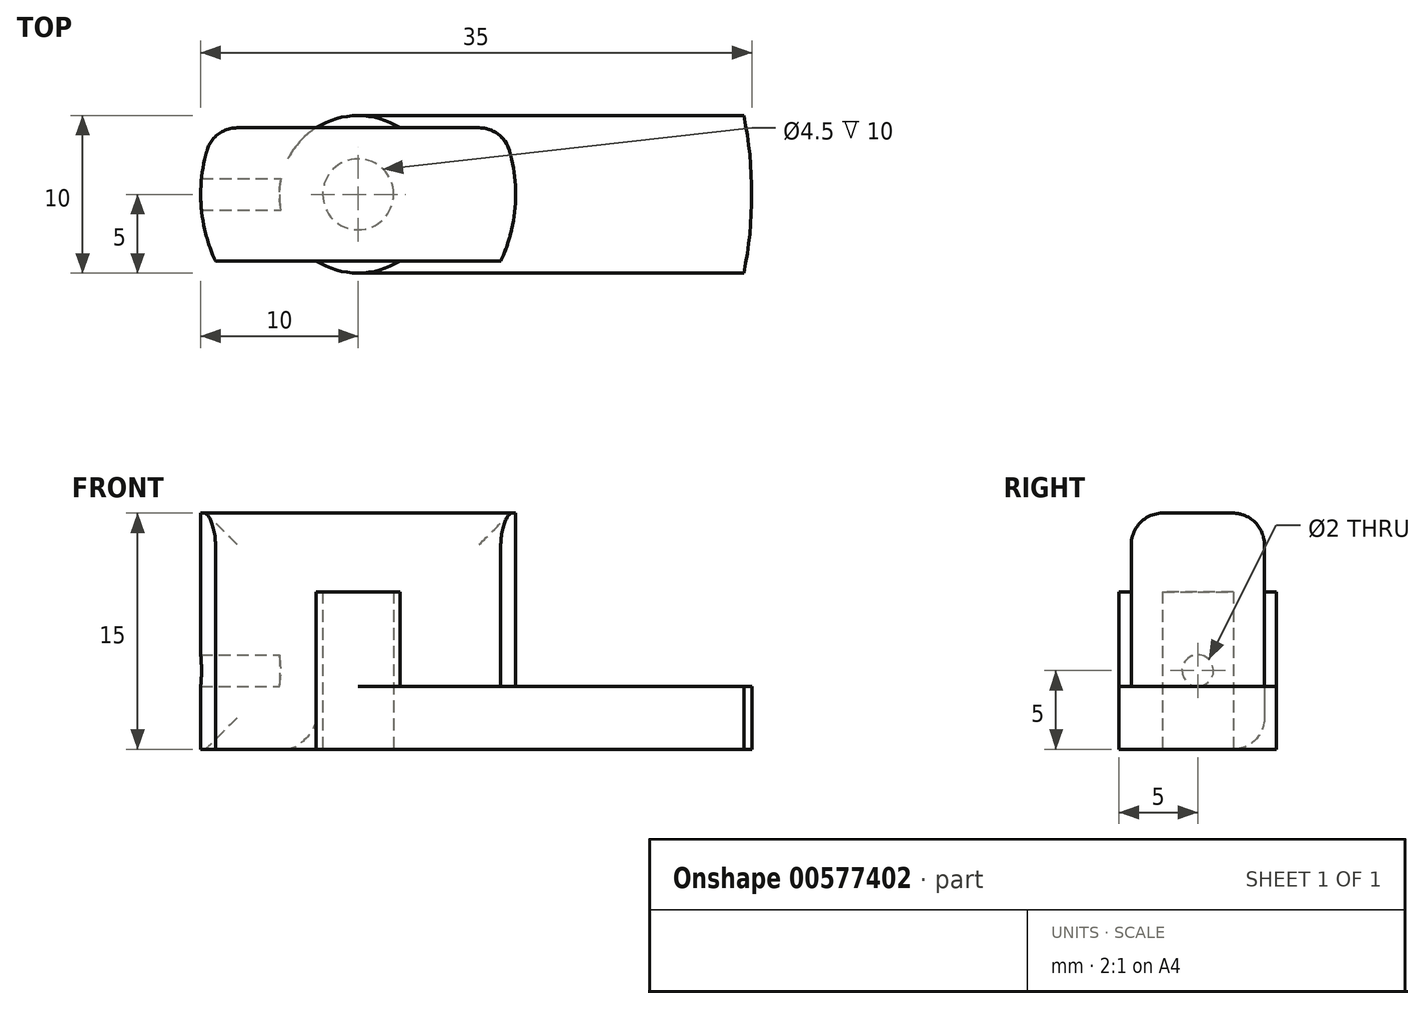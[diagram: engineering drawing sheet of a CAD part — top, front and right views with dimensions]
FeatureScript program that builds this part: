
annotation { "Feature Type Name" : "Feature", "Feature Type Description" : "" }
export const myFeature = defineFeature(function(context is Context, id is Id, definition is map)
    precondition{}
    {
        {
            var Q0;
            Q0=qCreatedBy(makeId("Top.planeOp"),FACE);
            var sketch = newSketch(context, id + "F0", { "sketchPlane" : qUnion([Q0])});
            skCircle(sketch, "E0", {"center": v(0, 0) * mm, "radius": 10 * mm});
            skLineSegment(sketch, "E1.bottom", {"start": v(12.74, -4.23) * mm, "end": v(-12.74, -4.23) * mm});
            skLineSegment(sketch, "E1.top", {"start": v(12.74, 4.23) * mm, "end": v(-12.74, 4.23) * mm});
            skLineSegment(sketch, "E1.left", {"start": v(12.74, -4.23) * mm, "end": v(12.74, 4.23) * mm});
            skLineSegment(sketch, "E1.right", {"start": v(-12.74, -4.23) * mm, "end": v(-12.74, 4.23) * mm});
            skCircle(sketch, "E2", {"center": v(0, 0) * mm, "radius": 2.5 * mm});
            skSolve(sketch);
        }
        {
            var Q0;
            {var subQ0=sQuery(id+"F0.wireOp",EDGE,"E1.top");var subQ1=sQuery(id+"F0.wireOp",EDGE,"E0");var subQ2=makeQuery(id+"F0.imprint","INTERSECT",VERTEX,{"disambiguationData":[OD(0.0)],"derivedFrom":[subQ1,subQ0]});Q0=makeQuery(id+"F0.imprint","IMPRINT",FACE,{"disambiguationData":[TD([[makeQuery(id+"F0.imprint","IMPRINT",EDGE,{"disambiguationData":[TD([[subQ2,1.0]])],"derivedFrom":subQ1}),1.0]])]});}
            var Q1;
            {var subQ0=sQuery(id+"F0.wireOp",EDGE,"E1.bottom");var subQ1=sQuery(id+"F0.wireOp",EDGE,"E0");var subQ2=makeQuery(id+"F0.imprint","INTERSECT",VERTEX,{"disambiguationData":[OD(0.0)],"derivedFrom":[subQ1,subQ0]});Q1=makeQuery(id+"F0.imprint","IMPRINT",FACE,{"disambiguationData":[TD([[makeQuery(id+"F0.imprint","IMPRINT",EDGE,{"disambiguationData":[TD([[subQ2,-1.0]])],"derivedFrom":subQ1}),1.0]])]});}
            extrude(context, id + "F1", {"entities" : qUnion([Q0, Q1]), "depth" : 3 * mm, "offsetDistance" : 25 * mm});
        }
        {
            var Q0;
            Q0=makeQuery(id+"F0.imprint","IMPRINT",FACE,{"disambiguationData":[TD([[makeQuery(id+"F0.imprint","IMPRINT",EDGE,{"derivedFrom":sQuery(id+"F0.wireOp",EDGE,"E2")}),-1.0]])]});
            var Q1;
            Q1=makeQuery(id+"F0.imprint","IMPRINT",FACE,{"disambiguationData":[TD([[makeQuery(id+"F0.imprint","IMPRINT",EDGE,{"derivedFrom":sQuery(id+"F0.wireOp",EDGE,"E2")}),1.0]])]});
            extrude(context, id + "F2", {"entities" : qUnion([Q0, Q1]), "operationType" : NewBodyOperationType.ADD, "depth" : 15 * mm, "offsetDistance" : 25 * mm});
        }
        {
            var Q0;
            Q0=makeQuery(id+"F0.imprint","IMPRINT",FACE,{"disambiguationData":[TD([[makeQuery(id+"F0.imprint","IMPRINT",EDGE,{"derivedFrom":sQuery(id+"F0.wireOp",EDGE,"E2")}),1.0]])]});
            extrude(context, id + "F3", {"entities" : qUnion([Q0]), "operationType" : NewBodyOperationType.REMOVE, "depth" : 10 * mm, "offsetDistance" : 25 * mm});
        }
        {
            var Q0;
            Q0=makeQuery(id+"F2.opExtrude","CAP_EDGE",EDGE,{"disambiguationData":[OSD([sQuery(id+"F0.wireOp",EDGE,"E1.top")])],"isStart":false});
            var Q1;
            Q1=makeQuery(id+"F2.opExtrude","CAP_EDGE",EDGE,{"disambiguationData":[OSD([sQuery(id+"F0.wireOp",EDGE,"E1.bottom")])],"isStart":false});
            var Q2;
            Q2=makeQuery(id+"F1.opExtrude","CAP_EDGE",EDGE,{"disambiguationData":[OSD([sQuery(id+"F0.wireOp",EDGE,"E1.bottom")])],"isStart":false});
            var Q3;
            Q3=makeQuery(id+"F2.opExtrude","SWEPT_FACE",FACE,{"disambiguationData":[OSD([sQuery(id+"F0.wireOp",EDGE,"E1.top")])]});
            var Q4;
            {var subQ0=sQuery(id+"F0.wireOp",EDGE,"E1.bottom");var subQ1=sQuery(id+"F0.wireOp",EDGE,"E0");Q4=makeQuery(id+"F1.opExtrude","CAP_EDGE",EDGE,{"disambiguationData":[OSD([subQ1]),TDD([makeQuery(id+"F0.imprint","IMPRINT",EDGE,{"disambiguationData":[TD([[makeQuery(id+"F0.imprint","INTERSECT",VERTEX,{"disambiguationData":[OD(0.0)],"derivedFrom":[subQ1,subQ0]}),-1.0]])],"derivedFrom":subQ1})])],"isStart":false});}
            var Q5;
            {var subQ0=sQuery(id+"F0.wireOp",EDGE,"E0");Q5=makeQuery(id+"F2.opExtrude","CAP_EDGE",EDGE,{"disambiguationData":[OSD([subQ0]),TDD([makeQuery(id+"F0.imprint","IMPRINT",EDGE,{"disambiguationData":[TD([[makeQuery(id+"F0.imprint","INTERSECT",VERTEX,{"disambiguationData":[OD(0.0)],"derivedFrom":[subQ0,sQuery(id+"F0.wireOp",EDGE,"E1.top")]}),-1.0]])],"derivedFrom":subQ0})])],"isStart":false});}
            var Q6;
            {var subQ0=sQuery(id+"F0.wireOp",EDGE,"E0");Q6=makeQuery(id+"F2.opExtrude","CAP_EDGE",EDGE,{"disambiguationData":[OSD([subQ0]),TDD([makeQuery(id+"F0.imprint","IMPRINT",EDGE,{"disambiguationData":[TD([[makeQuery(id+"F0.imprint","INTERSECT",VERTEX,{"disambiguationData":[OD(1.0)],"derivedFrom":[subQ0,sQuery(id+"F0.wireOp",EDGE,"E1.top")]}),1.0]])],"derivedFrom":subQ0})])],"isStart":false});}
            fillet(context, id + "F4", {"entities" : qUnion([Q0, Q1, Q2, Q3, Q4, Q5, Q6]), "radius" : 2 * mm, "tangentPropagation" : true, "allowEdgeOverflow" : false});
        }
        {
            var Q0;
            Q0=qCreatedBy(makeId("Right.planeOp"),FACE);
            var sketch = newSketch(context, id + "F5", { "sketchPlane" : qUnion([Q0])});
            skPoint(sketch, "E3.0", {"position": v(0, 0) * mm});
            skCircle(sketch, "E4", {"center": v(0, 5) * mm, "radius": 1 * mm});
            skSolve(sketch);
        }
        {
            var Q0;
            Q0=makeQuery(id+"F5.imprint","IMPRINT",FACE,{"disambiguationData":[TD([[makeQuery(id+"F5.imprint","IMPRINT",EDGE,{"derivedFrom":sQuery(id+"F5.wireOp",EDGE,"E4")}),1.0]])]});
            extrude(context, id + "F6", {"entities" : qUnion([Q0]), "operationType" : NewBodyOperationType.REMOVE, "oppositeDirection" : true, "depth" : 25 * mm, "offsetDistance" : 25 * mm});
        }
        {
            var Q0;
            Q0=qCreatedBy(makeId("Top.planeOp"),FACE);
            var sketch = newSketch(context, id + "F7", { "sketchPlane" : qUnion([Q0])});
            skCircle(sketch, "E5", {"center": v(0, 0) * mm, "radius": 5 * mm});
            skCircle(sketch, "E6", {"center": v(0, 0) * mm, "radius": 25 * mm});
            skLineSegment(sketch, "E7.bottom", {"start": v(25, 5) * mm, "end": v(-25, 5) * mm});
            skLineSegment(sketch, "E7.top", {"start": v(25, -5) * mm, "end": v(-25, -5) * mm});
            skLineSegment(sketch, "E7.left", {"start": v(25, 5) * mm, "end": v(25, -5) * mm});
            skLineSegment(sketch, "E7.right", {"start": v(-25, 5) * mm, "end": v(-25, -5) * mm});
            skCircle(sketch, "E8", {"center": v(0, 0) * mm, "radius": 2.25 * mm});
            skSolve(sketch);
        }
        {
            var Q0;
            Q0=makeQuery(id+"F7.imprint","IMPRINT",FACE,{"disambiguationData":[TD([[makeQuery(id+"F7.imprint","IMPRINT",EDGE,{"derivedFrom":sQuery(id+"F7.wireOp",EDGE,"E8")}),-1.0]])]});
            extrude(context, id + "F8", {"entities" : qUnion([Q0]), "depth" : 10 * mm, "offsetDistance" : 25 * mm});
        }
        {
            var Q0;
            {var subQ0=sQuery(id+"F7.wireOp",EDGE,"E7.bottom");var subQ3=sQuery(id+"F7.wireOp",EDGE,"E5");var subQ4=makeQuery(id+"F7.imprint","INTERSECT",VERTEX,{"derivedFrom":[subQ3,subQ0]});Q0=makeQuery(id+"F7.imprint","IMPRINT",FACE,{"disambiguationData":[TD([[makeQuery(id+"F7.imprint","IMPRINT",EDGE,{"disambiguationData":[TD([[subQ4,1.0]])],"derivedFrom":subQ3}),-1.0]])]});}
            extrude(context, id + "F9", {"entities" : qUnion([Q0]), "operationType" : NewBodyOperationType.ADD, "depth" : 4 * mm, "offsetDistance" : 25 * mm});
        }
    });
